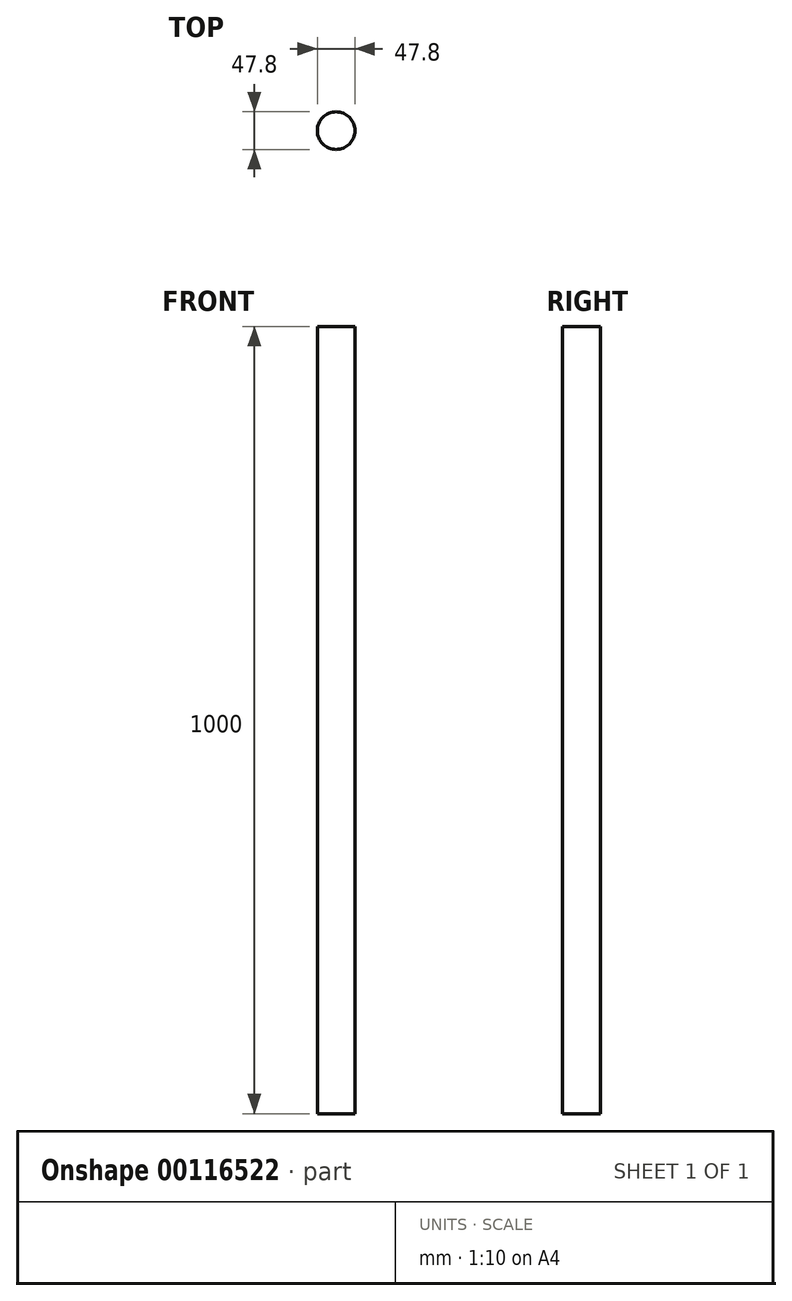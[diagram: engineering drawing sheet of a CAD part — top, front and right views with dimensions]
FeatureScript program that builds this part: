
annotation { "Feature Type Name" : "Feature", "Feature Type Description" : "" }
export const myFeature = defineFeature(function(context is Context, id is Id, definition is map)
    precondition{}
    {
        {
            var Q0;
            Q0=qCreatedBy(makeId("Top.planeOp"),FACE);
            var sketch = newSketch(context, id + "F0", { "sketchPlane" : qUnion([Q0])});
            skCircle(sketch, "E0", {"center": v(0, 0) * mm, "radius": 23.9 * mm});
            skSolve(sketch);
        }
        {
            var Q0;
            Q0=qSketchRegion(id+"F0",true);
            var Q1;
            Q1=makeQuery(id+"F0.imprint","IMPRINT",FACE,{"disambiguationData":[TD([[makeQuery(id+"F0.imprint","IMPRINT",EDGE,{"derivedFrom":sQuery(id+"F0.wireOp",EDGE,"E0")}),1.0]])]});
            extrude(context, id + "F1", {"entities" : qUnion([Q0, Q1]), "depth" : 1000 * mm});
        }
    });
